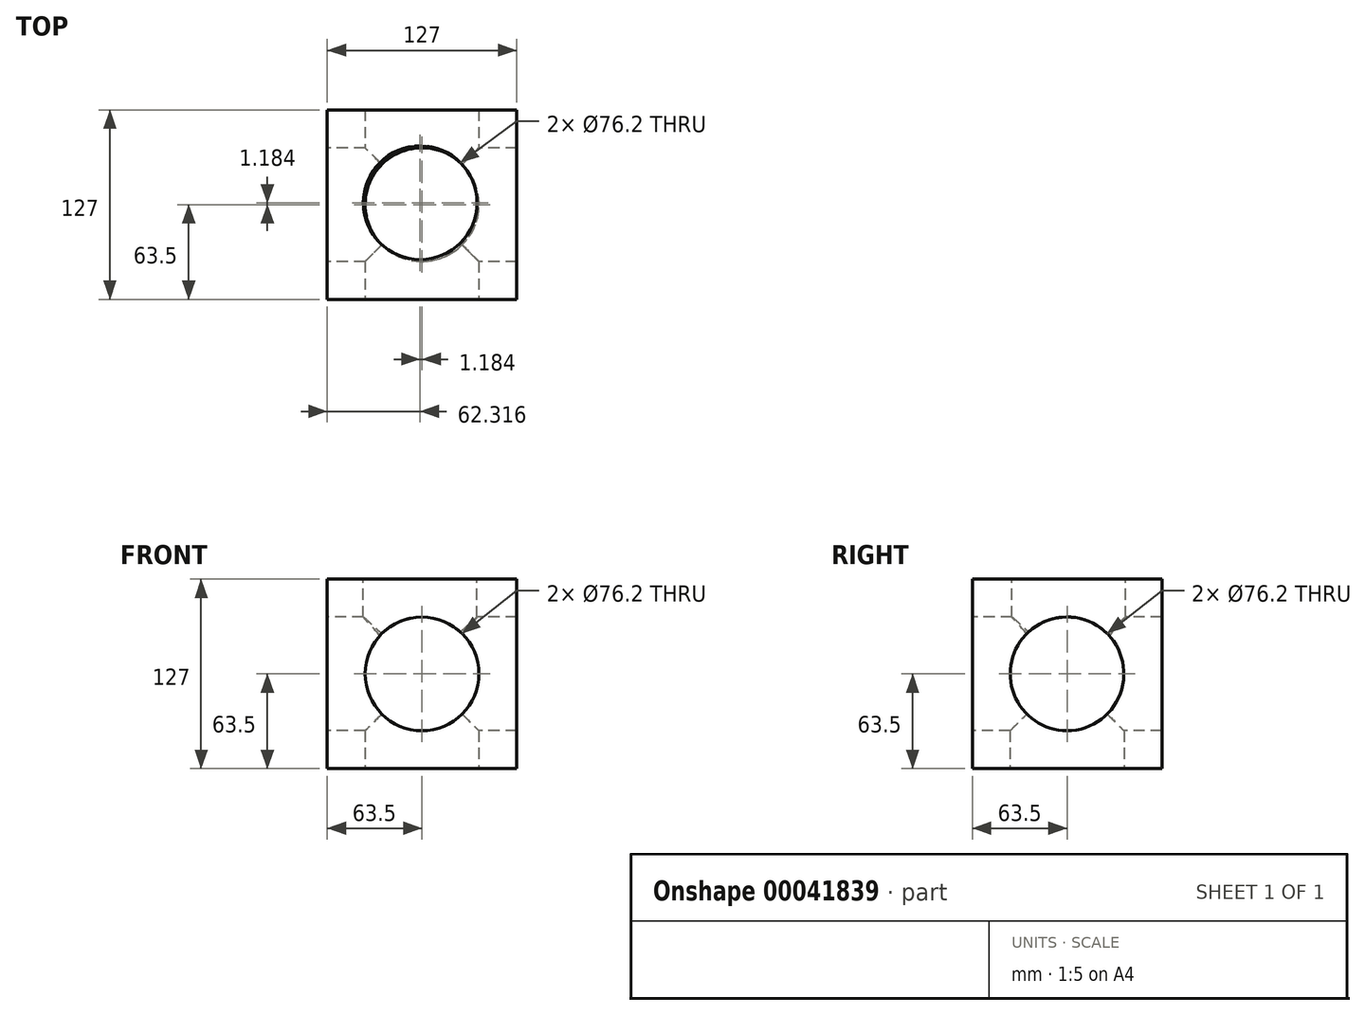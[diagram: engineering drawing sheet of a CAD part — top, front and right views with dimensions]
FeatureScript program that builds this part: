
annotation { "Feature Type Name" : "Feature", "Feature Type Description" : "" }
export const myFeature = defineFeature(function(context is Context, id is Id, definition is map)
    precondition{}
    {
        {
            var Q0;
            Q0=qCreatedBy(makeId("Front.planeOp"),FACE);
            var sketch = newSketch(context, id + "F0", { "sketchPlane" : qUnion([Q0])});
            skLineSegment(sketch, "E0", {"start": v(0, 0) * mm, "end": v(127, 0) * mm});
            skLineSegment(sketch, "E1", {"start": v(127, 0) * mm, "end": v(127, 127) * mm});
            skLineSegment(sketch, "E2", {"start": v(127, 127) * mm, "end": v(0, 127) * mm});
            skLineSegment(sketch, "E3", {"start": v(0, 127) * mm, "end": v(0, 0) * mm});
            skSolve(sketch);
        }
        {
            var Q0;
            Q0 = qSketchRegion(id + "F0", true);
            extrude(context, id + "F1", {"entities" : qUnion([Q0]), "depth" : 127 * mm});
        }
        {
            var Q0;
            Q0=makeQuery(id+"F1.opExtrude","CAP_FACE",FACE,{"disambiguationData":[OSD([sQuery(id+"F0.wireOp",EDGE,"E0"),sQuery(id+"F0.wireOp",EDGE,"E1"),sQuery(id+"F0.wireOp",EDGE,"E2"),sQuery(id+"F0.wireOp",EDGE,"E3")])],"isStart":false});
            var sketch = newSketch(context, id + "F2", { "sketchPlane" : qUnion([Q0])});
            skLineSegment(sketch, "E4", {"start": v(0, 0) * mm, "end": v(0, 127) * mm});
            skCircle(sketch, "E5", {"center": v(63.5, 63.5) * mm, "radius": 38.1 * mm});
            skSolve(sketch);
        }
        {
            var Q0;
            Q0=makeQuery(id+"F2.imprint","IMPRINT",FACE,{"disambiguationData":[TD([[makeQuery(id+"F2.imprint","IMPRINT",EDGE,{"derivedFrom":sQuery(id+"F2.wireOp",EDGE,"E5")}),1.0]])]});
            extrude(context, id + "F3", {"entities" : qUnion([Q0]), "operationType" : NewBodyOperationType.REMOVE, "oppositeDirection" : true, "depth" : 76.2 * mm});
        }
        {
            var Q0;
            Q0=makeQuery(id+"F1.opExtrude","SWEPT_FACE",FACE,{"disambiguationData":[OSD([sQuery(id+"F0.wireOp",EDGE,"E3")])]});
            var sketch = newSketch(context, id + "F4", { "sketchPlane" : qUnion([Q0])});
            skLineSegment(sketch, "E6", {"start": v(0, 0) * mm, "end": v(0, 127) * mm});
            skCircle(sketch, "E7", {"center": v(63.5, 63.5) * mm, "radius": 38.1 * mm});
            skSolve(sketch);
        }
        {
            var Q0;
            Q0=makeQuery(id+"F4.imprint","IMPRINT",FACE,{"disambiguationData":[TD([[makeQuery(id+"F4.imprint","IMPRINT",EDGE,{"derivedFrom":sQuery(id+"F4.wireOp",EDGE,"E7")}),1.0]])]});
            var sketch = newSketch(context, id + "F5", { "sketchPlane" : qUnion([Q0])});
            skSolve(sketch);
        }
        {
            var Q0;
            Q0 = qSketchRegion(id + "F5", true);
            var Q1;
            Q1=makeQuery(id+"F4.imprint","IMPRINT",FACE,{"disambiguationData":[TD([[makeQuery(id+"F4.imprint","IMPRINT",EDGE,{"derivedFrom":sQuery(id+"F4.wireOp",EDGE,"E7")}),1.0]])]});
            extrude(context, id + "F6", {"entities" : qUnion([Q0, Q1]), "operationType" : NewBodyOperationType.REMOVE, "oppositeDirection" : true, "depth" : 76.2 * mm});
        }
        {
            var Q0;
            Q0=makeQuery(id+"F1.opExtrude","SWEPT_FACE",FACE,{"disambiguationData":[OSD([sQuery(id+"F0.wireOp",EDGE,"E1")])]});
            var sketch = newSketch(context, id + "F7", { "sketchPlane" : qUnion([Q0])});
            skLineSegment(sketch, "E8", {"start": v(0, 0) * mm, "end": v(-127, 0) * mm});
            skCircle(sketch, "E9", {"center": v(-63.5, 63.5) * mm, "radius": 38.1 * mm});
            skPoint(sketch, "E9.perimeterSnap0", {"position": v(-63.5, 63.5) * mm});
            skSolve(sketch);
        }
        {
            var Q0;
            Q0=makeQuery(id+"F7.imprint","IMPRINT",FACE,{"disambiguationData":[TD([[makeQuery(id+"F7.imprint","IMPRINT",EDGE,{"derivedFrom":sQuery(id+"F7.wireOp",EDGE,"E9")}),1.0]])]});
            var sketch = newSketch(context, id + "F8", { "sketchPlane" : qUnion([Q0])});
            skSolve(sketch);
        }
        {
            var Q0;
            Q0 = qSketchRegion(id + "F8", true);
            var Q1;
            Q1=makeQuery(id+"F7.imprint","IMPRINT",FACE,{"disambiguationData":[TD([[makeQuery(id+"F7.imprint","IMPRINT",EDGE,{"derivedFrom":sQuery(id+"F7.wireOp",EDGE,"E9")}),1.0]])]});
            extrude(context, id + "F9", {"entities" : qUnion([Q0, Q1]), "operationType" : NewBodyOperationType.REMOVE, "oppositeDirection" : true, "depth" : 76.2 * mm});
        }
        {
            var Q0;
            Q0=makeQuery(id+"F1.opExtrude","CAP_FACE",FACE,{"disambiguationData":[OSD([sQuery(id+"F0.wireOp",EDGE,"E0"),sQuery(id+"F0.wireOp",EDGE,"E1"),sQuery(id+"F0.wireOp",EDGE,"E2"),sQuery(id+"F0.wireOp",EDGE,"E3")])],"isStart":true});
            var sketch = newSketch(context, id + "F10", { "sketchPlane" : qUnion([Q0])});
            skLineSegment(sketch, "E10", {"start": v(0, 0) * mm, "end": v(0, 127) * mm});
            skCircle(sketch, "E11", {"center": v(-63.5, 63.5) * mm, "radius": 38.1 * mm});
            skSolve(sketch);
        }
        {
            var Q0;
            Q0=makeQuery(id+"F10.imprint","IMPRINT",FACE,{"disambiguationData":[TD([[makeQuery(id+"F10.imprint","IMPRINT",EDGE,{"derivedFrom":sQuery(id+"F10.wireOp",EDGE,"E11")}),1.0]])]});
            extrude(context, id + "F11", {"entities" : qUnion([Q0]), "operationType" : NewBodyOperationType.REMOVE, "oppositeDirection" : true, "depth" : 76.2 * mm});
        }
        {
            var Q0;
            Q0=makeQuery(id+"F1.opExtrude","SWEPT_FACE",FACE,{"disambiguationData":[OSD([sQuery(id+"F0.wireOp",EDGE,"E2")])]});
            var sketch = newSketch(context, id + "F12", { "sketchPlane" : qUnion([Q0])});
            skCircle(sketch, "E12", {"center": v(62.32, -62.32) * mm, "radius": 38.1 * mm});
            skSolve(sketch);
        }
        {
            var Q0;
            Q0=makeQuery(id+"F12.imprint","IMPRINT",FACE,{"disambiguationData":[TD([[makeQuery(id+"F12.imprint","IMPRINT",EDGE,{"derivedFrom":sQuery(id+"F12.wireOp",EDGE,"E12")}),1.0]])]});
            extrude(context, id + "F13", {"entities" : qUnion([Q0]), "operationType" : NewBodyOperationType.REMOVE, "oppositeDirection" : true, "depth" : 76.2 * mm});
        }
        {
            var Q0;
            Q0=makeQuery(id+"F1.opExtrude","SWEPT_FACE",FACE,{"disambiguationData":[OSD([sQuery(id+"F0.wireOp",EDGE,"E0")])]});
            var sketch = newSketch(context, id + "F14", { "sketchPlane" : qUnion([Q0])});
            skCircle(sketch, "E13", {"center": v(63.5, 63.5) * mm, "radius": 38.1 * mm});
            skSolve(sketch);
        }
        {
            var Q0;
            Q0=makeQuery(id+"F14.imprint","IMPRINT",FACE,{"disambiguationData":[TD([[makeQuery(id+"F14.imprint","IMPRINT",EDGE,{"derivedFrom":sQuery(id+"F14.wireOp",EDGE,"E13")}),1.0]])]});
            extrude(context, id + "F15", {"entities" : qUnion([Q0]), "operationType" : NewBodyOperationType.REMOVE, "oppositeDirection" : true, "depth" : 76.2 * mm});
        }
    });
